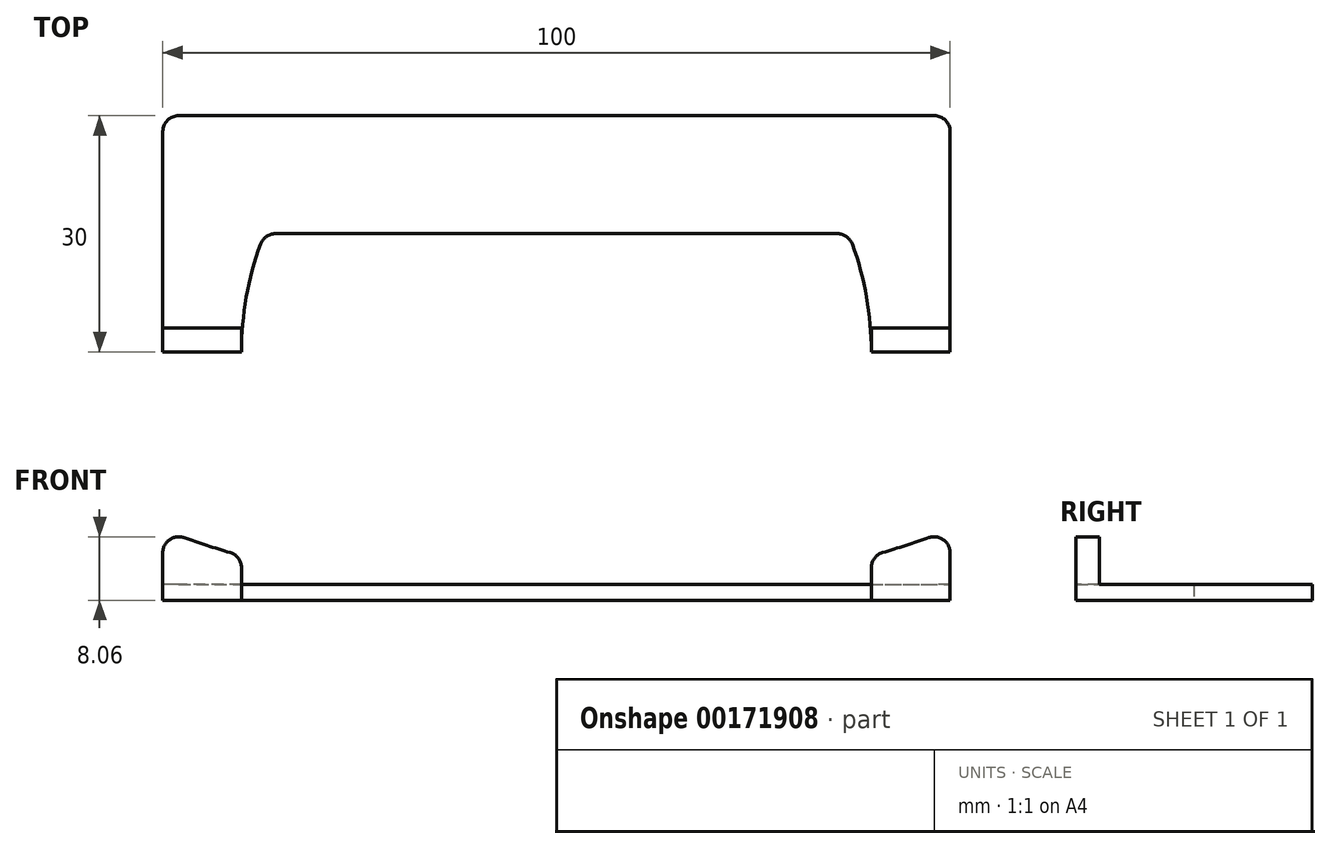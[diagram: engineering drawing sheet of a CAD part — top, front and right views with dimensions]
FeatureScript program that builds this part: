
annotation { "Feature Type Name" : "Feature", "Feature Type Description" : "" }
export const myFeature = defineFeature(function(context is Context, id is Id, definition is map)
    precondition{}
    {
        {
            var Q0;
            Q0=qCreatedBy(makeId("Top.planeOp"),FACE);
            var sketch = newSketch(context, id + "F0", { "sketchPlane" : qUnion([Q0])});
            skLineSegment(sketch, "E0.bottom", {"start": v(-50, 15) * mm, "end": v(50, 15) * mm});
            skLineSegment(sketch, "E0.top", {"start": v(-50, -15) * mm, "end": v(-40, -15) * mm});
            skLineSegment(sketch, "E0.left", {"start": v(-50, 15) * mm, "end": v(-50, -15) * mm});
            skLineSegment(sketch, "E0.right", {"start": v(50, 15) * mm, "end": v(50, -15) * mm});
            skPoint(sketch, "E0.middle", {"position": v(0, 0) * mm});
            skArc(sketch, "E1", {"start": v(-37.08, 0) * mm, "mid": v(-39.26, -7.36) * mm, "end": v(-40, -15) * mm});
            skLineSegment(sketch, "E2", {"start": v(-37.08, 0) * mm, "end": v(37.08, 0) * mm});
            skLineSegment(sketch, "E3.trimOffspring", {"start": v(40, -15) * mm, "end": v(50, -15) * mm});
            skArc(sketch, "E4.trimOffspring", {"start": v(40, -15) * mm, "mid": v(39.26, -7.36) * mm, "end": v(37.08, 0) * mm});
            skSolve(sketch);
        }
        {
            var Q0;
            Q0 = qSketchRegion(id + "F0", true);
            extrude(context, id + "F1", {"entities" : qUnion([Q0]), "depth" : 2 * mm});
        }
        {
            var Q0;
            Q0=makeQuery(id+"F1.opExtrude","CAP_FACE",FACE,{"disambiguationData":[OSD([sQuery(id+"F0.wireOp",EDGE,"E0.bottom"),sQuery(id+"F0.wireOp",EDGE,"E0.top"),sQuery(id+"F0.wireOp",EDGE,"E0.left"),sQuery(id+"F0.wireOp",EDGE,"E0.right"),sQuery(id+"F0.wireOp",EDGE,"E1"),sQuery(id+"F0.wireOp",EDGE,"E2"),sQuery(id+"F0.wireOp",EDGE,"E3.trimOffspring"),sQuery(id+"F0.wireOp",EDGE,"E4.trimOffspring")])],"isStart":false});
            var sketch = newSketch(context, id + "F2", { "sketchPlane" : qUnion([Q0])});
            skLineSegment(sketch, "E5.bottom", {"start": v(-40, -15) * mm, "end": v(-50, -15) * mm});
            skLineSegment(sketch, "E5.top", {"start": v(-40, -12) * mm, "end": v(-50, -12) * mm});
            skLineSegment(sketch, "E5.left", {"start": v(-40, -15) * mm, "end": v(-40, -12) * mm});
            skLineSegment(sketch, "E5.right", {"start": v(-50, -15) * mm, "end": v(-50, -12) * mm});
            skLineSegment(sketch, "E6.MirrorCS", {"start": v(40, -12) * mm, "end": v(50, -12) * mm});
            skLineSegment(sketch, "E7.MirrorCS", {"start": v(40, -15) * mm, "end": v(50, -15) * mm});
            skLineSegment(sketch, "E8.MirrorCS", {"start": v(40, -15) * mm, "end": v(40, -12) * mm});
            skLineSegment(sketch, "E9.MirrorCS", {"start": v(50, -15) * mm, "end": v(50, -12) * mm});
            skSolve(sketch);
        }
        {
            var Q0;
            Q0 = qSketchRegion(id + "F2", true);
            extrude(context, id + "F3", {"entities" : qUnion([Q0]), "operationType" : NewBodyOperationType.ADD, "depth" : 10 * mm});
        }
        {
            var Q0;
            Q0=qCreatedBy(makeId("Front.planeOp"),FACE);
            var sketch = newSketch(context, id + "F4", { "sketchPlane" : qUnion([Q0])});
            skCircle(sketch, "E10", {"center": v(0, 145) * mm, "radius": 145 * mm});
            skSolve(sketch);
        }
        {
            var Q0;
            Q0 = qSketchRegion(id + "F4", true);
            extrude(context, id + "F5", {"entities" : qUnion([Q0]), "operationType" : NewBodyOperationType.REMOVE, "depth" : 25 * mm});
        }
        {
            var Q0;
            Q0=makeQuery(id+"F5.boolean.opBoolean","INTERSECT",EDGE,{"derivedFrom":[makeQuery(id+"F3.boolean.opBoolean","MERGE",FACE,{"derivedFrom":[makeQuery(id+"F1.opExtrude","SWEPT_FACE",FACE,{"disambiguationData":[OSD([sQuery(id+"F0.wireOp",EDGE,"E0.left")])]}),makeQuery(id+"F3.opExtrude","SWEPT_FACE",FACE,{"disambiguationData":[OSD([sQuery(id+"F2.wireOp",EDGE,"E5.right")])]})]}),makeQuery(id+"F5.opExtrude","SWEPT_FACE",FACE,{"disambiguationData":[OSD([sQuery(id+"F4.wireOp",EDGE,"E10")])]})]});
            var Q1;
            Q1=makeQuery(id+"F5.boolean.opBoolean","INTERSECT",EDGE,{"derivedFrom":[makeQuery(id+"F3.boolean.opBoolean","MERGE",FACE,{"derivedFrom":[makeQuery(id+"F1.opExtrude","SWEPT_FACE",FACE,{"disambiguationData":[OSD([sQuery(id+"F0.wireOp",EDGE,"E0.right")])]}),makeQuery(id+"F3.opExtrude","SWEPT_FACE",FACE,{"disambiguationData":[OSD([sQuery(id+"F2.wireOp",EDGE,"E9.MirrorCS")])]})]}),makeQuery(id+"F5.opExtrude","SWEPT_FACE",FACE,{"disambiguationData":[OSD([sQuery(id+"F4.wireOp",EDGE,"E10")])]})]});
            var Q2;
            Q2=makeQuery(id+"F5.boolean.opBoolean","INTERSECT",EDGE,{"derivedFrom":[makeQuery(id+"F3.opExtrude","SWEPT_FACE",FACE,{"disambiguationData":[OSD([sQuery(id+"F2.wireOp",EDGE,"E5.left")])]}),makeQuery(id+"F5.opExtrude","SWEPT_FACE",FACE,{"disambiguationData":[OSD([sQuery(id+"F4.wireOp",EDGE,"E10")])]})]});
            var Q3;
            Q3=makeQuery(id+"F5.boolean.opBoolean","INTERSECT",EDGE,{"derivedFrom":[makeQuery(id+"F3.opExtrude","SWEPT_FACE",FACE,{"disambiguationData":[OSD([sQuery(id+"F2.wireOp",EDGE,"E8.MirrorCS")])]}),makeQuery(id+"F5.opExtrude","SWEPT_FACE",FACE,{"disambiguationData":[OSD([sQuery(id+"F4.wireOp",EDGE,"E10")])]})]});
            var Q4;
            Q4=makeQuery(id+"F1.opExtrude","SWEPT_EDGE",EDGE,{"disambiguationData":[OSD([sQuery(id+"F0.wireOp",EDGE,"E2"),sQuery(id+"F0.wireOp",EDGE,"E4.trimOffspring")])]});
            var Q5;
            Q5=makeQuery(id+"F1.opExtrude","SWEPT_EDGE",EDGE,{"disambiguationData":[OSD([sQuery(id+"F0.wireOp",EDGE,"E1"),sQuery(id+"F0.wireOp",EDGE,"E2")])]});
            var Q6;
            Q6=makeQuery(id+"F1.opExtrude","SWEPT_EDGE",EDGE,{"disambiguationData":[OSD([sQuery(id+"F0.wireOp",EDGE,"E0.bottom"),sQuery(id+"F0.wireOp",EDGE,"E0.left")])]});
            var Q7;
            Q7=makeQuery(id+"F1.opExtrude","SWEPT_EDGE",EDGE,{"disambiguationData":[OSD([sQuery(id+"F0.wireOp",EDGE,"E0.bottom"),sQuery(id+"F0.wireOp",EDGE,"E0.right")])]});
            fillet(context, id + "F6", {"entities" : qUnion([Q0, Q1, Q2, Q3, Q4, Q5, Q6, Q7]), "radius" : 2 * mm, "tangentPropagation" : true, "allowEdgeOverflow" : false});
        }
    });
